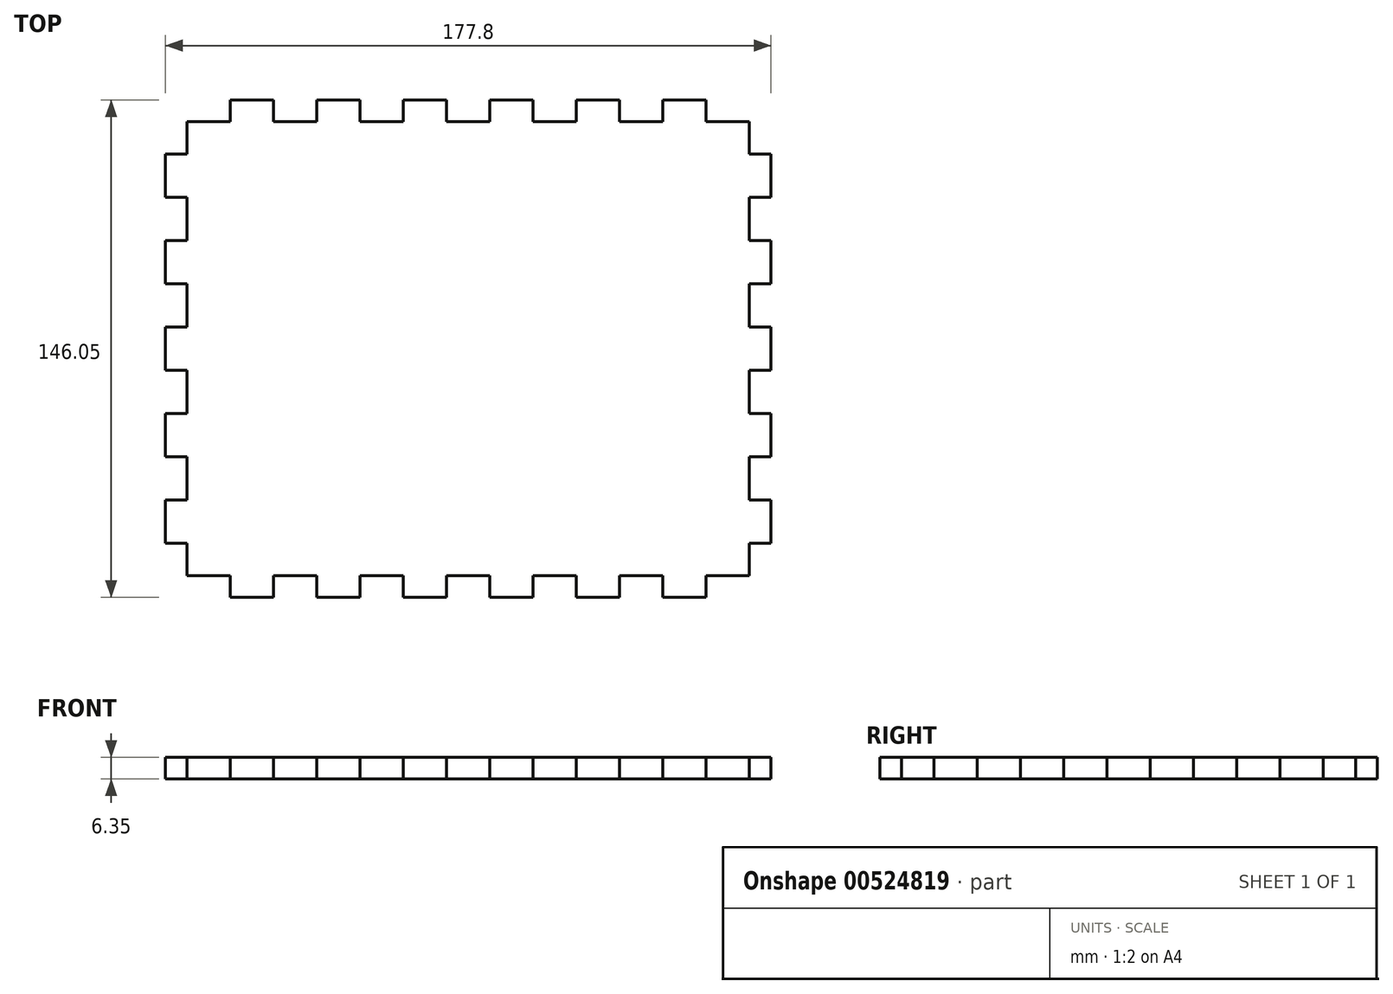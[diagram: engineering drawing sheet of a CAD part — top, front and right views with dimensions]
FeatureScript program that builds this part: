
annotation { "Feature Type Name" : "Feature", "Feature Type Description" : "" }
export const myFeature = defineFeature(function(context is Context, id is Id, definition is map)
    precondition{}
    {
        {
            var Q0;
            Q0=qCreatedBy(makeId("Top.planeOp"),FACE);
            var sketch = newSketch(context, id + "F0", { "sketchPlane" : qUnion([Q0])});
            skLineSegment(sketch, "E0.bottom", {"start": v(19.05, 0) * mm, "end": v(31.75, 0) * mm});
            skLineSegment(sketch, "E0.left", {"start": v(0, 0) * mm, "end": v(0, -28.58) * mm});
            skLineSegment(sketch, "E1", {"start": v(6.35, -6.35) * mm, "end": v(19.05, -6.35) * mm});
            skLineSegment(sketch, "E2", {"start": v(19.05, -6.35) * mm, "end": v(19.05, 0) * mm});
            skLineSegment(sketch, "E3", {"start": v(31.75, 0) * mm, "end": v(31.75, -6.35) * mm});
            skLineSegment(sketch, "E4", {"start": v(31.75, -6.35) * mm, "end": v(44.45, -6.35) * mm});
            skLineSegment(sketch, "E5", {"start": v(44.45, -6.35) * mm, "end": v(44.45, 0) * mm});
            skLineSegment(sketch, "E6", {"start": v(44.45, 0) * mm, "end": v(57.15, 0) * mm});
            skLineSegment(sketch, "E7", {"start": v(57.15, 0) * mm, "end": v(57.15, -6.35) * mm});
            skLineSegment(sketch, "E8", {"start": v(57.15, -6.35) * mm, "end": v(69.85, -6.35) * mm});
            skLineSegment(sketch, "E9", {"start": v(69.85, -6.35) * mm, "end": v(69.85, 0) * mm});
            skLineSegment(sketch, "E10.trimOffspring", {"start": v(69.85, 0) * mm, "end": v(82.55, 0) * mm});
            skLineSegment(sketch, "E11", {"start": v(82.55, 0) * mm, "end": v(82.55, -6.35) * mm});
            skLineSegment(sketch, "E12", {"start": v(82.55, -6.35) * mm, "end": v(95.25, -6.35) * mm});
            skLineSegment(sketch, "E13", {"start": v(95.25, -6.35) * mm, "end": v(95.25, 0) * mm});
            skLineSegment(sketch, "E14", {"start": v(95.25, 0) * mm, "end": v(107.95, 0) * mm});
            skLineSegment(sketch, "E15", {"start": v(107.95, 0) * mm, "end": v(107.95, -6.35) * mm});
            skLineSegment(sketch, "E16", {"start": v(107.95, -6.35) * mm, "end": v(120.65, -6.35) * mm});
            skLineSegment(sketch, "E17", {"start": v(120.65, -6.35) * mm, "end": v(120.65, 0) * mm});
            skLineSegment(sketch, "E18.trimOffspring", {"start": v(120.65, 0) * mm, "end": v(133.35, 0) * mm});
            skLineSegment(sketch, "E19", {"start": v(133.35, 0) * mm, "end": v(133.35, -6.35) * mm});
            skLineSegment(sketch, "E20", {"start": v(133.35, -6.35) * mm, "end": v(146.05, -6.35) * mm});
            skLineSegment(sketch, "E21", {"start": v(146.05, -6.35) * mm, "end": v(146.05, 0) * mm});
            skLineSegment(sketch, "E22", {"start": v(146.05, 0) * mm, "end": v(158.75, 0) * mm});
            skLineSegment(sketch, "E23", {"start": v(158.75, 0) * mm, "end": v(158.75, -6.35) * mm});
            skLineSegment(sketch, "E24", {"start": v(158.75, -6.35) * mm, "end": v(171.45, -6.35) * mm});
            skPoint(sketch, "E25.orphan", {"position": v(177.8, 0) * mm});
            skLineSegment(sketch, "E26", {"start": v(6.35, -6.35) * mm, "end": v(6.35, -15.88) * mm});
            skLineSegment(sketch, "E27", {"start": v(6.35, -15.88) * mm, "end": v(0, -15.88) * mm});
            skLineSegment(sketch, "E28", {"start": v(0, -15.88) * mm, "end": v(0, -28.58) * mm});
            skLineSegment(sketch, "E29", {"start": v(0, -28.58) * mm, "end": v(6.35, -28.58) * mm});
            skLineSegment(sketch, "E30", {"start": v(6.35, -28.58) * mm, "end": v(6.35, -41.28) * mm});
            skLineSegment(sketch, "E31", {"start": v(6.35, -41.28) * mm, "end": v(0, -41.28) * mm});
            skLineSegment(sketch, "E32", {"start": v(0, -41.28) * mm, "end": v(0, -53.98) * mm});
            skLineSegment(sketch, "E33", {"start": v(0, -53.98) * mm, "end": v(6.35, -53.98) * mm});
            skLineSegment(sketch, "E34", {"start": v(6.35, -53.98) * mm, "end": v(6.35, -66.68) * mm});
            skLineSegment(sketch, "E35", {"start": v(6.35, -66.68) * mm, "end": v(0, -66.68) * mm});
            skLineSegment(sketch, "E36", {"start": v(0, -66.68) * mm, "end": v(0, -79.38) * mm});
            skLineSegment(sketch, "E37", {"start": v(0, -79.38) * mm, "end": v(6.35, -79.38) * mm});
            skLineSegment(sketch, "E38", {"start": v(6.35, -79.38) * mm, "end": v(6.35, -92.08) * mm});
            skLineSegment(sketch, "E39", {"start": v(6.35, -92.08) * mm, "end": v(0, -92.08) * mm});
            skLineSegment(sketch, "E40", {"start": v(0, -92.08) * mm, "end": v(0, -104.78) * mm});
            skLineSegment(sketch, "E41", {"start": v(0, -104.78) * mm, "end": v(6.35, -104.78) * mm});
            skLineSegment(sketch, "E42", {"start": v(6.35, -104.78) * mm, "end": v(6.35, -117.48) * mm});
            skLineSegment(sketch, "E43", {"start": v(6.35, -117.48) * mm, "end": v(0, -117.48) * mm});
            skLineSegment(sketch, "E44", {"start": v(0, -117.48) * mm, "end": v(0, -130.18) * mm});
            skLineSegment(sketch, "E45", {"start": v(0, -130.18) * mm, "end": v(6.35, -130.18) * mm});
            skLineSegment(sketch, "E46", {"start": v(6.35, -130.18) * mm, "end": v(6.35, -139.7) * mm});
            skLineSegment(sketch, "E47", {"start": v(6.35, -139.7) * mm, "end": v(19.05, -139.7) * mm});
            skLineSegment(sketch, "E48", {"start": v(19.05, -139.7) * mm, "end": v(19.05, -139.7) * mm});
            skPoint(sketch, "E49.orphan", {"position": v(0, -146.05) * mm});
            skLineSegment(sketch, "E50", {"start": v(88.9, -6.35) * mm, "end": v(88.9, -38.89) * mm, "construction": true});
            skLineSegment(sketch, "E51", {"start": v(0, -73.03) * mm, "end": v(49.25, -73.03) * mm, "construction": true});
            skLineSegment(sketch, "E52.MirrorCS", {"start": v(171.45, -6.35) * mm, "end": v(171.45, -15.88) * mm});
            skLineSegment(sketch, "E53.MirrorCS", {"start": v(171.45, -15.88) * mm, "end": v(177.8, -15.88) * mm});
            skLineSegment(sketch, "E54.MirrorCS", {"start": v(177.8, -15.88) * mm, "end": v(177.8, -28.58) * mm});
            skLineSegment(sketch, "E55.MirrorCS", {"start": v(177.8, -28.58) * mm, "end": v(171.45, -28.58) * mm});
            skLineSegment(sketch, "E56.MirrorCS", {"start": v(171.45, -28.58) * mm, "end": v(171.45, -41.28) * mm});
            skLineSegment(sketch, "E57.MirrorCS", {"start": v(177.8, -41.28) * mm, "end": v(177.8, -53.98) * mm});
            skLineSegment(sketch, "E58.MirrorCS", {"start": v(177.8, -53.98) * mm, "end": v(171.45, -53.98) * mm});
            skLineSegment(sketch, "E59.MirrorCS", {"start": v(171.45, -53.98) * mm, "end": v(171.45, -66.68) * mm});
            skLineSegment(sketch, "E60.MirrorCS", {"start": v(171.45, -66.68) * mm, "end": v(177.8, -66.68) * mm});
            skLineSegment(sketch, "E61.MirrorCS", {"start": v(177.8, -66.68) * mm, "end": v(177.8, -79.38) * mm});
            skLineSegment(sketch, "E62.MirrorCS", {"start": v(177.8, -79.38) * mm, "end": v(171.45, -79.38) * mm});
            skLineSegment(sketch, "E63.MirrorCS", {"start": v(171.45, -79.38) * mm, "end": v(171.45, -92.08) * mm});
            skLineSegment(sketch, "E64.MirrorCS", {"start": v(171.45, -92.08) * mm, "end": v(177.8, -92.08) * mm});
            skLineSegment(sketch, "E65.MirrorCS", {"start": v(177.8, -92.08) * mm, "end": v(177.8, -104.78) * mm});
            skLineSegment(sketch, "E66.MirrorCS", {"start": v(177.8, -104.78) * mm, "end": v(171.45, -104.78) * mm});
            skLineSegment(sketch, "E67.MirrorCS", {"start": v(171.45, -104.78) * mm, "end": v(171.45, -117.48) * mm});
            skLineSegment(sketch, "E68.MirrorCS", {"start": v(171.45, -117.48) * mm, "end": v(177.8, -117.48) * mm});
            skLineSegment(sketch, "E69.MirrorCS", {"start": v(177.8, -117.48) * mm, "end": v(177.8, -130.18) * mm});
            skLineSegment(sketch, "E70.MirrorCS", {"start": v(177.8, -130.18) * mm, "end": v(171.45, -130.18) * mm});
            skLineSegment(sketch, "E71.MirrorCS", {"start": v(171.45, -130.18) * mm, "end": v(171.45, -139.7) * mm});
            skLineSegment(sketch, "E72.MirrorCS", {"start": v(171.45, -139.7) * mm, "end": v(158.75, -139.7) * mm});
            skLineSegment(sketch, "E73.MirrorCS", {"start": v(158.75, -139.7) * mm, "end": v(158.75, -139.7) * mm});
            skLineSegment(sketch, "E74.MirrorCS", {"start": v(19.05, -146.05) * mm, "end": v(31.75, -146.05) * mm});
            skLineSegment(sketch, "E75.MirrorCS", {"start": v(31.75, -146.05) * mm, "end": v(31.75, -139.7) * mm});
            skLineSegment(sketch, "E76.MirrorCS", {"start": v(31.75, -139.7) * mm, "end": v(44.45, -139.7) * mm});
            skLineSegment(sketch, "E77.MirrorCS", {"start": v(44.45, -139.7) * mm, "end": v(44.45, -146.05) * mm});
            skLineSegment(sketch, "E78.MirrorCS", {"start": v(44.45, -146.05) * mm, "end": v(57.15, -146.05) * mm});
            skLineSegment(sketch, "E79.MirrorCS", {"start": v(57.15, -146.05) * mm, "end": v(57.15, -139.7) * mm});
            skLineSegment(sketch, "E80.MirrorCS", {"start": v(57.15, -139.7) * mm, "end": v(69.85, -139.7) * mm});
            skLineSegment(sketch, "E81.MirrorCS", {"start": v(69.85, -139.7) * mm, "end": v(69.85, -146.05) * mm});
            skLineSegment(sketch, "E82.MirrorCS", {"start": v(69.85, -146.05) * mm, "end": v(82.55, -146.05) * mm});
            skLineSegment(sketch, "E83.MirrorCS", {"start": v(82.55, -146.05) * mm, "end": v(82.55, -139.7) * mm});
            skLineSegment(sketch, "E84.MirrorCS", {"start": v(82.55, -139.7) * mm, "end": v(95.25, -139.7) * mm});
            skLineSegment(sketch, "E85.MirrorCS", {"start": v(95.25, -139.7) * mm, "end": v(95.25, -146.05) * mm});
            skLineSegment(sketch, "E86.MirrorCS", {"start": v(95.25, -146.05) * mm, "end": v(107.95, -146.05) * mm});
            skLineSegment(sketch, "E87.MirrorCS", {"start": v(107.95, -146.05) * mm, "end": v(107.95, -139.7) * mm});
            skLineSegment(sketch, "E88.MirrorCS", {"start": v(107.95, -139.7) * mm, "end": v(120.65, -139.7) * mm});
            skLineSegment(sketch, "E89.MirrorCS", {"start": v(120.65, -139.7) * mm, "end": v(120.65, -146.05) * mm});
            skLineSegment(sketch, "E90.MirrorCS", {"start": v(120.65, -146.05) * mm, "end": v(133.35, -146.05) * mm});
            skLineSegment(sketch, "E91.MirrorCS", {"start": v(133.35, -139.7) * mm, "end": v(146.05, -139.7) * mm});
            skLineSegment(sketch, "E92.MirrorCS", {"start": v(146.05, -139.7) * mm, "end": v(146.05, -146.05) * mm});
            skLineSegment(sketch, "E93.MirrorCS", {"start": v(146.05, -146.05) * mm, "end": v(158.75, -146.05) * mm});
            skLineSegment(sketch, "E94.MirrorCS", {"start": v(158.75, -146.05) * mm, "end": v(158.75, -139.7) * mm});
            skLineSegment(sketch, "E95", {"start": v(177.8, -41.28) * mm, "end": v(171.45, -41.28) * mm});
            skLineSegment(sketch, "E96", {"start": v(133.35, -139.7) * mm, "end": v(133.35, -146.05) * mm});
            skLineSegment(sketch, "E97", {"start": v(19.05, -139.7) * mm, "end": v(19.05, -146.05) * mm});
            skSolve(sketch);
        }
        {
            var Q0;
            Q0=makeQuery(id+"F0.imprint","IMPRINT",FACE,{"disambiguationData":[TD([[makeQuery(id+"F0.imprint","IMPRINT",EDGE,{"derivedFrom":sQuery(id+"F0.wireOp",EDGE,"E1")}),-1.0]])]});
            extrude(context, id + "F1", {"entities" : qUnion([Q0]), "depth" : 6.35 * mm, "offsetDistance" : 25.4 * mm});
        }
    });
